# Revit family: Furniture_Other_Sjobergs_Sewing_Table_Lift
name_source: partatom
category: Furniture
revit_build: Autodesk Revit 2017 (Build: 20190508_0315(x64)
units: mm (PartAtom-declared; Revit-internal decimal feet)

## family parameters
Always vertical = Yes
Cut with Voids When Loaded = No
OmniClass Number = 23.40.50.11
OmniClass Title = Educational, Entertainment Equipment and Furnishings
Room Calculation Point = No
Shared = No
Work Plane-Based = No

## types (1)
- Sewing Table w/ Lift
    AssetType = Movable
    BIMObjectName = Furniture_Other_Sjobergs_Sewing_Table_Lift
    Brand = Sjöbergs
    Category = School, textile craft
    Color = Wooden
    ConvergoRefNr = 0184-2005-0008-SE
    Cost = 0 $
    Features = The sewing machine can be raised and lowered
    IfcExportAs = IfcFurnishingElementType
    IfcExportType = TABLE
    MainColor = Wooden
    ManufacterURL = https://www.sjobergs.se
    Manufacturer = Sjöbergs
    ManufacturerName = Sjöbergs
    Material = Wood
    Model = Sewing Table w/ Lift
    ModelNumber = 33060
    Name = Sjobergs_Sewing_Table_Lift
    NominalDepth = 600 mm  [stored 1.9685 ft]
    NominalHeight = 897 mm
    NominalWidth = 1200 mm
    ProductDatasheet = https://www.sjobergs.se
    ProductInformation = A complete sewing machine table consisting of table top 33105 in grey laminate. Legs 33106 in birch with electric lift. Footboard in grey laminate. Cable channel 33212 and extension cord 33213 are included.
    SewingTableMainMaterial = Beech
    SewingTableSecondaryMaterial = Aluminum
    SewingTableTertiaryMaterial = Grey laminate
    Shape = Rectangular
    Size = 600x1200x897 mm
    URL = https://www.sjobergs.se
    Version = 1
    VersionDate = 30/06/2020
    Weight = 54 kg

note: [stored X ft] marks values corroborated as IEEE doubles in the binary element streams (Revit-internal decimal feet)

## geometry (parser evidence)
native form markers: Sweep x4
no freeform markers — native parametric forms only
